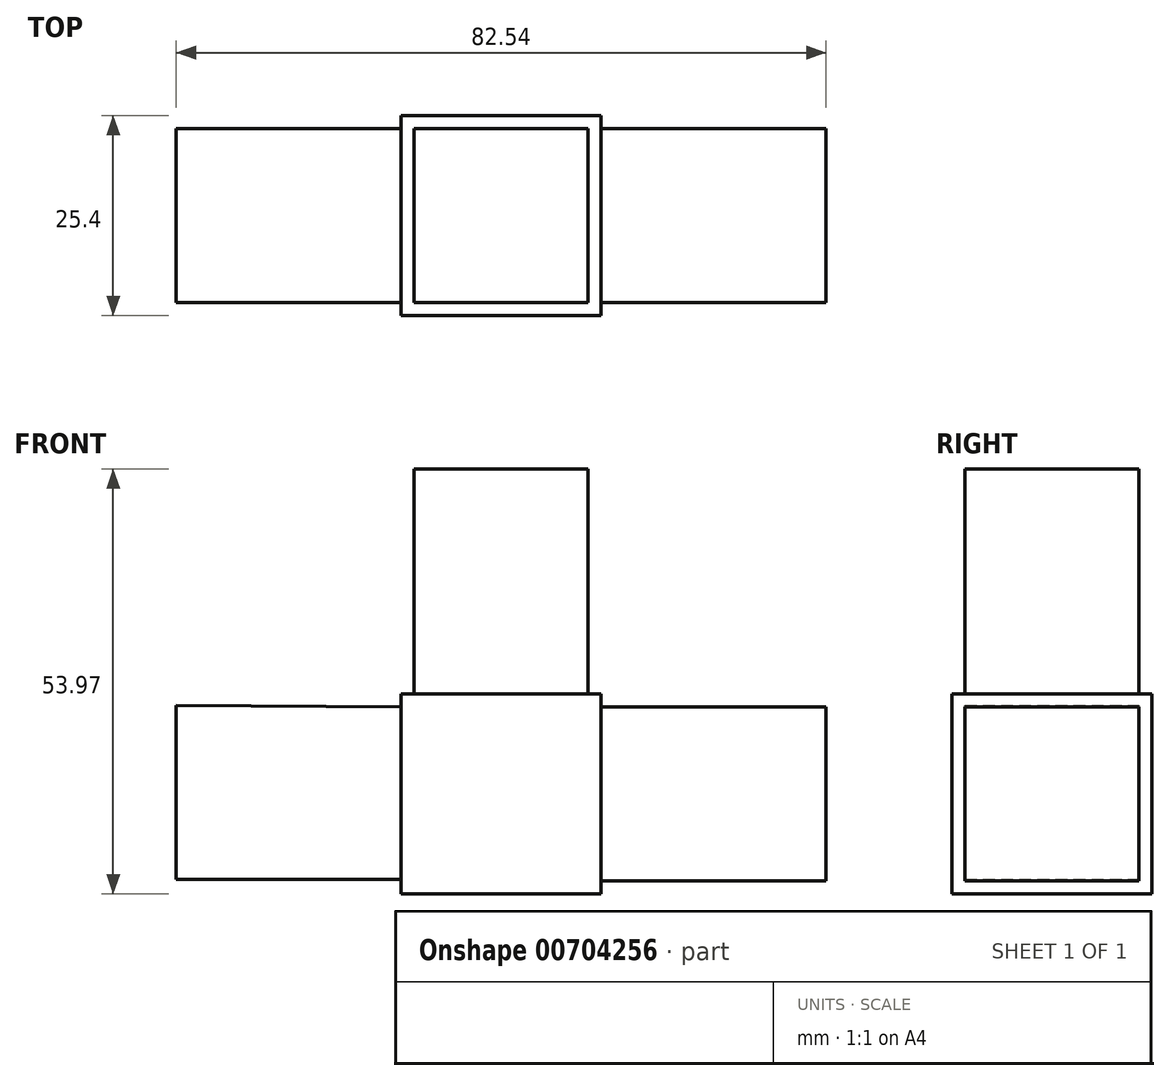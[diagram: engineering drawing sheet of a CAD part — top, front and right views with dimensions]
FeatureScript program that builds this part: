
annotation { "Feature Type Name" : "Feature", "Feature Type Description" : "" }
export const myFeature = defineFeature(function(context is Context, id is Id, definition is map)
    precondition{}
    {
        {
            var Q0;
            Q0=qCreatedBy(makeId("Front.planeOp"),FACE);
            var sketch = newSketch(context, id + "F0", { "sketchPlane" : qUnion([Q0])});
            skLineSegment(sketch, "E0.bottom", {"start": v(-12.7, 12.7) * mm, "end": v(12.7, 12.7) * mm});
            skLineSegment(sketch, "E0.top", {"start": v(-12.7, -12.7) * mm, "end": v(12.7, -12.7) * mm});
            skLineSegment(sketch, "E0.left", {"start": v(-12.7, 12.7) * mm, "end": v(-12.7, -12.7) * mm});
            skLineSegment(sketch, "E0.right", {"start": v(12.7, 12.7) * mm, "end": v(12.7, -12.7) * mm});
            skPoint(sketch, "E0.middle", {"position": v(0, 0) * mm});
            skLineSegment(sketch, "E1", {"start": v(12.7, 11.05) * mm, "end": v(41.28, 11.05) * mm});
            skLineSegment(sketch, "E2", {"start": v(41.28, 11.05) * mm, "end": v(41.28, -11.05) * mm});
            skLineSegment(sketch, "E3", {"start": v(41.28, -11.05) * mm, "end": v(12.7, -11.05) * mm});
            skLineSegment(sketch, "E4", {"start": v(-11.05, 12.7) * mm, "end": v(-11.05, 41.27) * mm});
            skLineSegment(sketch, "E5", {"start": v(-11.05, 41.27) * mm, "end": v(11.05, 41.27) * mm});
            skLineSegment(sketch, "E6", {"start": v(11.05, 41.27) * mm, "end": v(11.05, 12.7) * mm});
            skLineSegment(sketch, "E7", {"start": v(-12.7, -10.84) * mm, "end": v(-41.27, -10.84) * mm});
            skLineSegment(sketch, "E8", {"start": v(-41.27, -10.84) * mm, "end": v(-41.27, 11.26) * mm});
            skLineSegment(sketch, "E9", {"start": v(-41.27, 11.26) * mm, "end": v(-12.7, 11.05) * mm});
            skSolve(sketch);
        }
        {
            var Q0;
            {var subQ0=sQuery(id+"F0.wireOp",EDGE,"E0.top");Q0=makeQuery(id+"F0.imprint","IMPRINT",FACE,{"disambiguationData":[TD([[makeQuery(id+"F0.imprint","IMPRINT",EDGE,{"derivedFrom":subQ0}),1.0]])]});}
            extrude(context, id + "F1", {"entities" : qUnion([Q0]), "endBound" : BoundingType.SYMMETRIC, "depth" : 25.4 * mm, "offsetDistance" : 25.4 * mm});
        }
        {
            var Q0;
            {var subQ0=sQuery(id+"F0.wireOp",EDGE,"E7");Q0=makeQuery(id+"F0.imprint","IMPRINT",FACE,{"disambiguationData":[TD([[makeQuery(id+"F0.imprint","IMPRINT",EDGE,{"derivedFrom":subQ0}),-1.0]])]});}
            var Q1;
            {var subQ0=sQuery(id+"F0.wireOp",EDGE,"E4");Q1=makeQuery(id+"F0.imprint","IMPRINT",FACE,{"disambiguationData":[TD([[makeQuery(id+"F0.imprint","IMPRINT",EDGE,{"derivedFrom":subQ0}),-1.0]])]});}
            var Q2;
            {var subQ0=sQuery(id+"F0.wireOp",EDGE,"E1");Q2=makeQuery(id+"F0.imprint","IMPRINT",FACE,{"disambiguationData":[TD([[makeQuery(id+"F0.imprint","IMPRINT",EDGE,{"derivedFrom":subQ0}),-1.0]])]});}
            extrude(context, id + "F2", {"entities" : qUnion([Q0, Q1, Q2]), "operationType" : NewBodyOperationType.ADD, "endBound" : BoundingType.SYMMETRIC, "depth" : 22.1 * mm, "offsetDistance" : 25.4 * mm});
        }
    });
